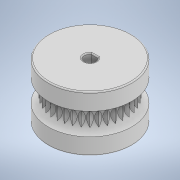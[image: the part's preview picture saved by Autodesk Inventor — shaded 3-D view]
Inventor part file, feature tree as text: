
AUTODESK INVENTOR PART (.ipt)
format: ipt  version: 2021 (Build 250183000, 183)  size: 385,024 bytes
history: native  units: in
note: dims shown in document units (in); Inventor stores cm internally (conversion verified against a paired STEP export)
features: sketch x5, extrude x4, fillet x2, revolve x1, mirror x1, pattern_circular x1, projected_geometry x1
ambient origin geometry x8: Origin, YZ Plane, XZ Plane, XY Plane, X Axis, Y Axis, Z Axis, Center Point
bodies: Solid1 (feature_tree)
feature tree (15):
  revolve  "Revolution1"  [1 undecoded]
  mirror  "Mirror1"
  fillet  "Fillet1"  Radius=0.0591in
  extrude  "Extrusion1"  TaperAngle=90.0deg  [1 undecoded]
  extrude  "Extrusion2"  Depth=0.1969in
  extrude  "Extrusion3"  Depth=0.4823in TaperAngle=0.0deg
  fillet  "Fillet2"  Radius=0.315in
  extrude  "Extrusion4"  Depth=0.5118in
  pattern_circular  "Circular Pattern1"  [2 undecoded]
  sketch  "Sketch1"  dims[d0=0.7087in d1=0.4724in d3=0.0591in]
  sketch  "Sketch2"  dims[d4=0.1969in d5=90.0deg]
  sketch  "Sketch3"  dims[d6=0.0197in d7=0.1969in]
  sketch  "Sketch4"  dims[d8=0.0787in d9=0.4823in d10=0.0in d11=0.315in]
  sketch  "Sketch5"  dims[d12=0.4626in d13=0.0in d14=0.5118in d15=0.2756in d16=0.0in d17=0.0197in d18=1.1417in d19=0.8661in d20=0.8661in d21=0.4331in d22=0.4331in d23=0.4331in d24=0.0in d25=0.8661in d26=0.8661in d27=0.8661in d28=0.4331in d29=0.9449in d30=0.0in d31=14.1732in d32=360.0deg]
  projected_geometry  "Projected Loop1"
note: 4 required parameter values undecoded (feature->parameter linkage not recoverable at this tier; creation-order binding heuristic only, values carry confidence <= 0.55)